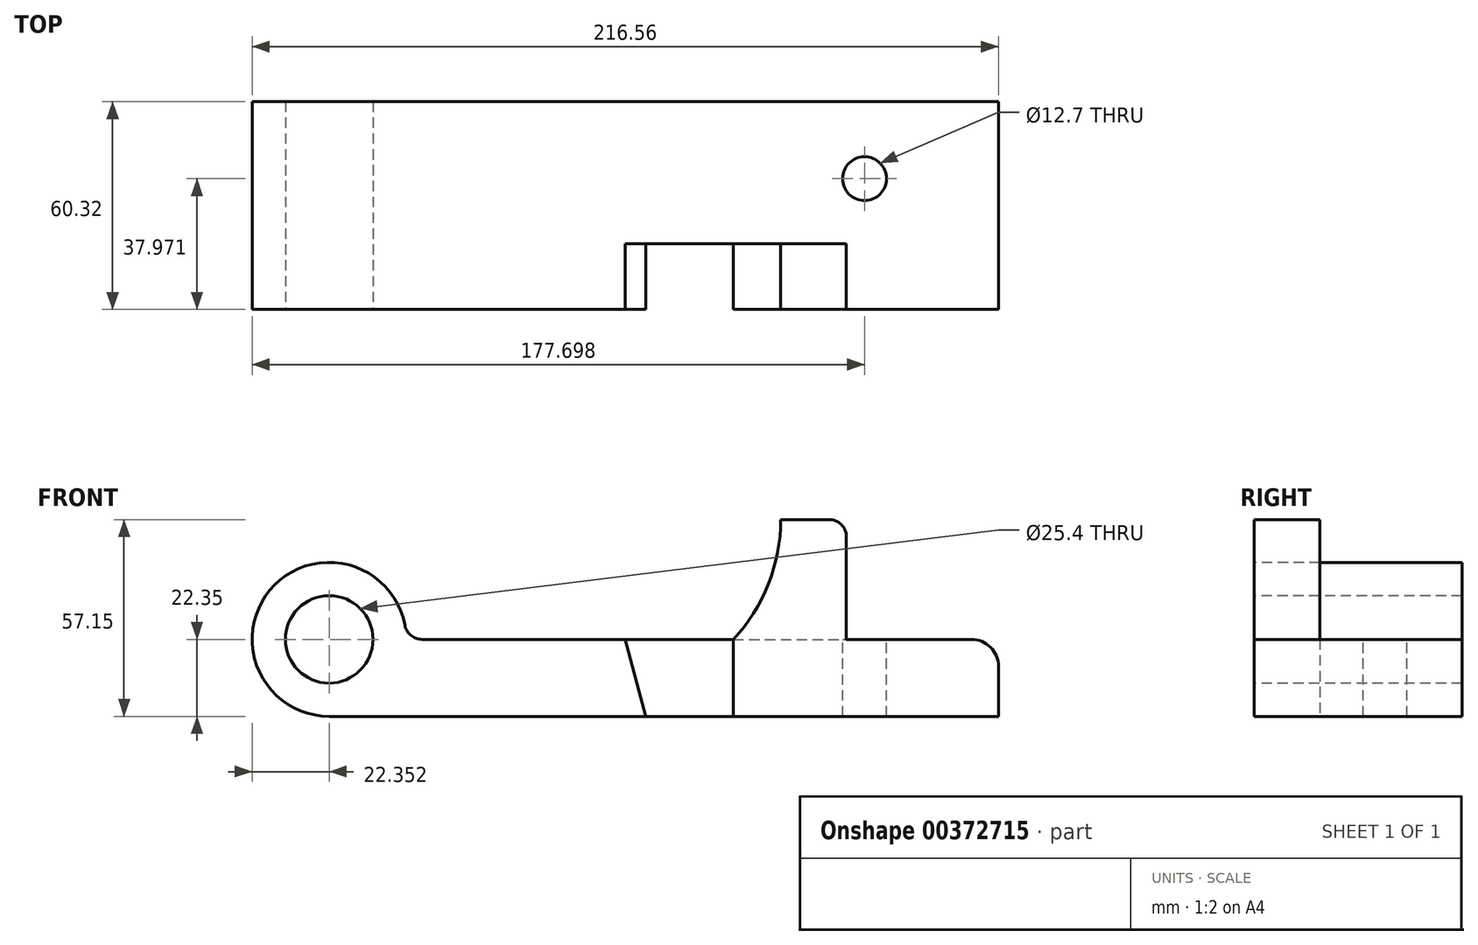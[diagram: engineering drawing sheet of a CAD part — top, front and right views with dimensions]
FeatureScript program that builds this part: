
annotation { "Feature Type Name" : "Feature", "Feature Type Description" : "" }
export const myFeature = defineFeature(function(context is Context, id is Id, definition is map)
    precondition{}
    {
        {
            var Q0;
            Q0=qCreatedBy(makeId("Front.planeOp"),FACE);
            var sketch = newSketch(context, id + "F0", { "sketchPlane" : qUnion([Q0])});
            skArc(sketch, "E0", {"start": v(-63.58, 0) * mm, "mid": v(-101.73, 15.8) * mm, "end": v(-85.93, -22.35) * mm});
            skCircle(sketch, "E1", {"center": v(-85.93, 0) * mm, "radius": 12.7 * mm});
            skLineSegment(sketch, "E2.bottom", {"start": v(-85.93, -22.35) * mm, "end": v(108.28, -22.35) * mm});
            skLineSegment(sketch, "E2.top", {"start": v(-63.58, 0) * mm, "end": v(100.4, 0) * mm});
            skLineSegment(sketch, "E2.right", {"start": v(108.28, -22.35) * mm, "end": v(108.28, -7.87) * mm});
            skPoint(sketch, "E3.visualSharp", {"position": v(108.28, 0) * mm});
            skArc(sketch, "E3.filletArc", {"start": v(108.28, -7.87) * mm, "mid": v(105.97, -2.3) * mm, "end": v(100.4, 0) * mm});
            skSolve(sketch);
        }
        {
            var Q0;
            Q0 = qSketchRegion(id + "F0", true);
            extrude(context, id + "F1", {"entities" : qUnion([Q0]), "endBound" : BoundingType.SYMMETRIC, "oppositeDirection" : true, "depth" : 60.32 * mm});
        }
        {
            var Q0;
            Q0=makeQuery(id+"F1.opExtrude","CAP_FACE",FACE,{"disambiguationData":[OSD([sQuery(id+"F0.wireOp",EDGE,"E0"),sQuery(id+"F0.wireOp",EDGE,"E1"),sQuery(id+"F0.wireOp",EDGE,"E2.bottom"),sQuery(id+"F0.wireOp",EDGE,"E2.top"),sQuery(id+"F0.wireOp",EDGE,"E2.right"),sQuery(id+"F0.wireOp",EDGE,"E3.filletArc")])],"isStart":true});
            var sketch = newSketch(context, id + "F2", { "sketchPlane" : qUnion([Q0])});
            skLineSegment(sketch, "E4", {"start": v(-0.08, 0) * mm, "end": v(5.92, -22.35) * mm});
            skLineSegment(sketch, "E5", {"start": v(5.92, -22.35) * mm, "end": v(31.32, -22.35) * mm});
            skLineSegment(sketch, "E6", {"start": v(31.32, -22.35) * mm, "end": v(31.32, 0) * mm});
            skLineSegment(sketch, "E7", {"start": v(31.32, 0) * mm, "end": v(-0.08, 0) * mm});
            skCircle(sketch, "E8.0", {"center": v(-85.93, 0) * mm, "radius": 12.7 * mm});
            skSolve(sketch);
        }
        {
            var Q0;
            Q0=makeQuery(id+"F2.imprint","IMPRINT",FACE,{"disambiguationData":[TD([[makeQuery(id+"F2.imprint","IMPRINT",EDGE,{"derivedFrom":sQuery(id+"F2.wireOp",EDGE,"E4")}),1.0]])]});
            extrude(context, id + "F3", {"entities" : qUnion([Q0]), "operationType" : NewBodyOperationType.REMOVE, "oppositeDirection" : true, "depth" : 19.05 * mm});
        }
        {
            var Q0;
            {var subQ0=sQuery(id+"F0.wireOp",EDGE,"E3.filletArc");var subQ1=sQuery(id+"F0.wireOp",EDGE,"E2.right");var subQ2=sQuery(id+"F0.wireOp",EDGE,"E2.top");var subQ3=sQuery(id+"F0.wireOp",EDGE,"E2.bottom");Q0=makeQuery(id+"F3.boolean.opBoolean","SPLIT",FACE,{"disambiguationData":[TD([makeQuery(id+"F1.opExtrude","SWEPT_FACE",FACE,{"disambiguationData":[OSD([subQ1])]})])],"derivedFrom":makeQuery(id+"F1.opExtrude","CAP_FACE",FACE,{"disambiguationData":[OSD([sQuery(id+"F0.wireOp",EDGE,"E0"),sQuery(id+"F0.wireOp",EDGE,"E1"),subQ3,subQ2,subQ1,subQ0])],"isStart":true})});}
            var sketch = newSketch(context, id + "F4", { "sketchPlane" : qUnion([Q0])});
            skLineSegment(sketch, "E9.top", {"start": v(59.08, 34.8) * mm, "end": v(45.11, 34.8) * mm});
            skLineSegment(sketch, "E9.left", {"start": v(64.16, 0) * mm, "end": v(64.16, 29.72) * mm});
            skArc(sketch, "E10", {"start": v(31.32, 0) * mm, "mid": v(41.54, 16.08) * mm, "end": v(45.11, 34.8) * mm});
            skLineSegment(sketch, "E11", {"start": v(64.16, 0) * mm, "end": v(31.32, 0) * mm});
            skCircle(sketch, "E12.0", {"center": v(-85.93, 0) * mm, "radius": 12.7 * mm});
            skPoint(sketch, "E13.visualSharp", {"position": v(64.16, 34.8) * mm});
            skArc(sketch, "E13.filletArc", {"start": v(64.16, 29.72) * mm, "mid": v(62.67, 33.31) * mm, "end": v(59.08, 34.8) * mm});
            skSolve(sketch);
        }
        {
            var Q0;
            Q0=makeQuery(id+"F4.imprint","IMPRINT",FACE,{"disambiguationData":[TD([[makeQuery(id+"F4.imprint","IMPRINT",EDGE,{"derivedFrom":sQuery(id+"F4.wireOp",EDGE,"E9.top")}),1.0]])]});
            extrude(context, id + "F5", {"entities" : qUnion([Q0]), "operationType" : NewBodyOperationType.ADD, "oppositeDirection" : true, "depth" : 19.05 * mm});
        }
        {
            var Q0;
            Q0=makeQuery(id+"F1.opExtrude","SWEPT_FACE",FACE,{"disambiguationData":[OSD([sQuery(id+"F0.wireOp",EDGE,"E2.top")])]});
            var sketch = newSketch(context, id + "F6", { "sketchPlane" : qUnion([Q0])});
            skCircle(sketch, "E14", {"center": v(69.42, 7.81) * mm, "radius": 6.35 * mm});
            skSolve(sketch);
        }
        {
            var Q0;
            Q0 = qSketchRegion(id + "F6", true);
            extrude(context, id + "F7", {"entities" : qUnion([Q0]), "operationType" : NewBodyOperationType.REMOVE, "endBound" : BoundingType.THROUGH_ALL, "oppositeDirection" : true, "depth" : 25.4 * mm});
        }
        {
            var Q0;
            Q0=makeQuery(id+"F1.opExtrude","SWEPT_EDGE",EDGE,{"disambiguationData":[OSD([sQuery(id+"F0.wireOp",EDGE,"E0"),sQuery(id+"F0.wireOp",EDGE,"E2.top")])]});
            fillet(context, id + "F8", {"entities" : qUnion([Q0]), "radius" : 5.08 * mm, "tangentPropagation" : true, "allowEdgeOverflow" : false});
        }
    });
